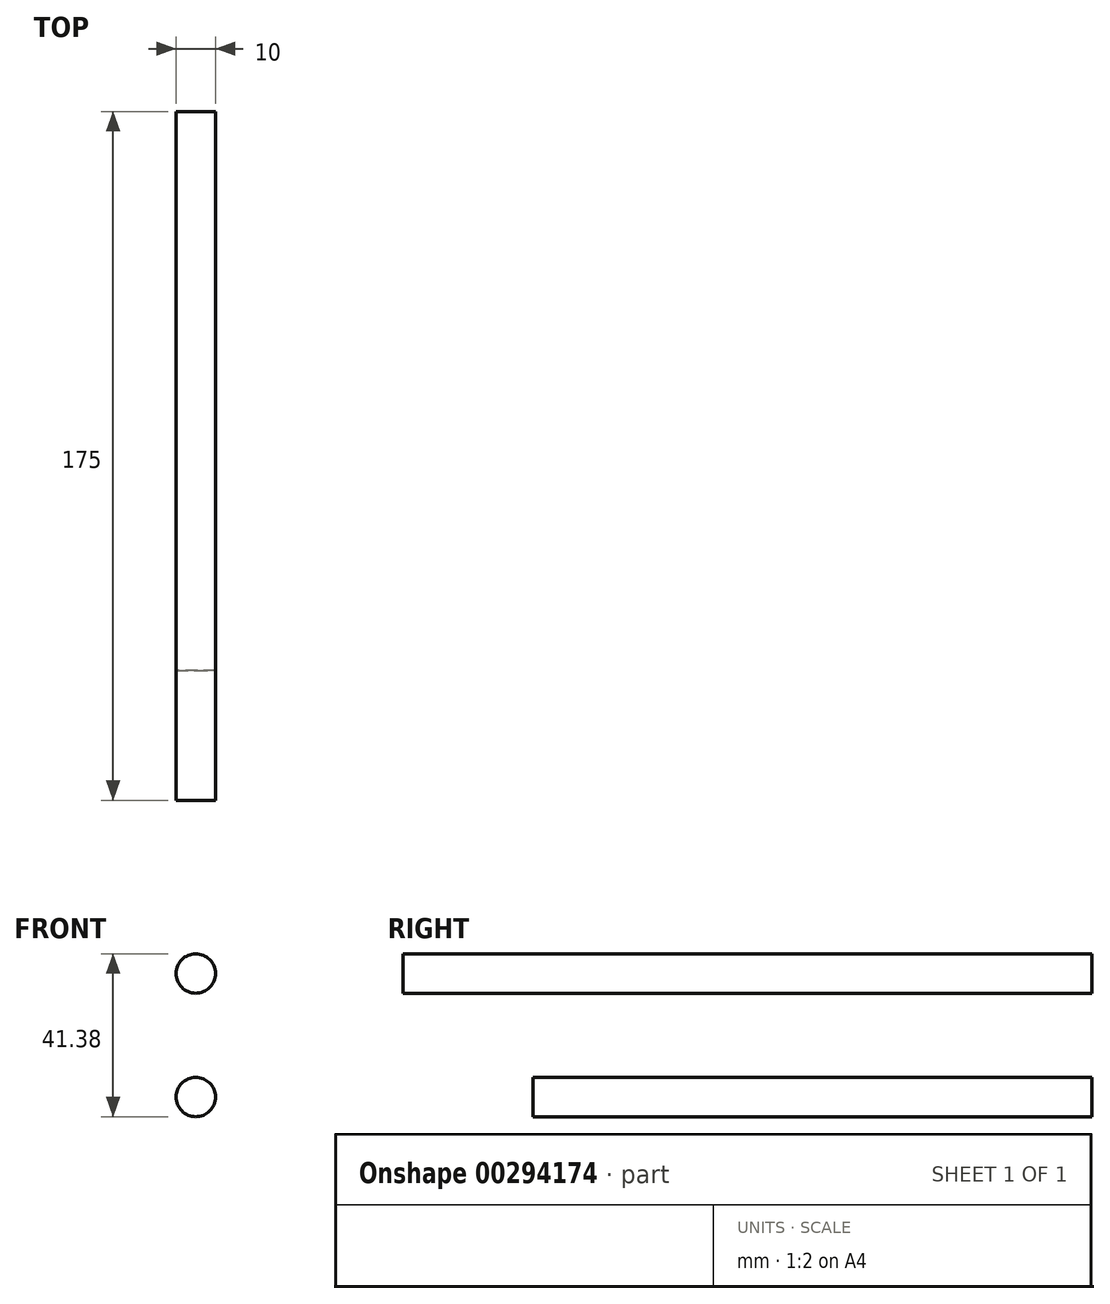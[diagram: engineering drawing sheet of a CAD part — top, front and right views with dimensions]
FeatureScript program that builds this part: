
annotation { "Feature Type Name" : "Feature", "Feature Type Description" : "" }
export const myFeature = defineFeature(function(context is Context, id is Id, definition is map)
    precondition{}
    {
        {
            var Q0;
            Q0=qCreatedBy(makeId("Front.planeOp"),FACE);
            var sketch = newSketch(context, id + "F0", { "sketchPlane" : qUnion([Q0])});
            skCircle(sketch, "E0", {"center": v(0, 0) * mm, "radius": 5 * mm});
            skSolve(sketch);
        }
        {
            var Q0;
            Q0 = qSketchRegion(id + "F0", true);
            extrude(context, id + "F1", {"entities" : qUnion([Q0]), "depth" : 142 * mm});
        }
        {
            var Q0;
            Q0=qCreatedBy(makeId("Front.planeOp"),FACE);
            var sketch = newSketch(context, id + "F2", { "sketchPlane" : qUnion([Q0])});
            skCircle(sketch, "E1", {"center": v(0, 31.38) * mm, "radius": 5 * mm});
            skSolve(sketch);
        }
        {
            var Q0;
            Q0=makeQuery(id+"F2.imprint","IMPRINT",FACE,{"disambiguationData":[TD([[makeQuery(id+"F2.imprint","IMPRINT",EDGE,{"derivedFrom":sQuery(id+"F2.wireOp",EDGE,"E1")}),1.0]])]});
            extrude(context, id + "F3", {"entities" : qUnion([Q0]), "depth" : 175 * mm});
        }
    });
